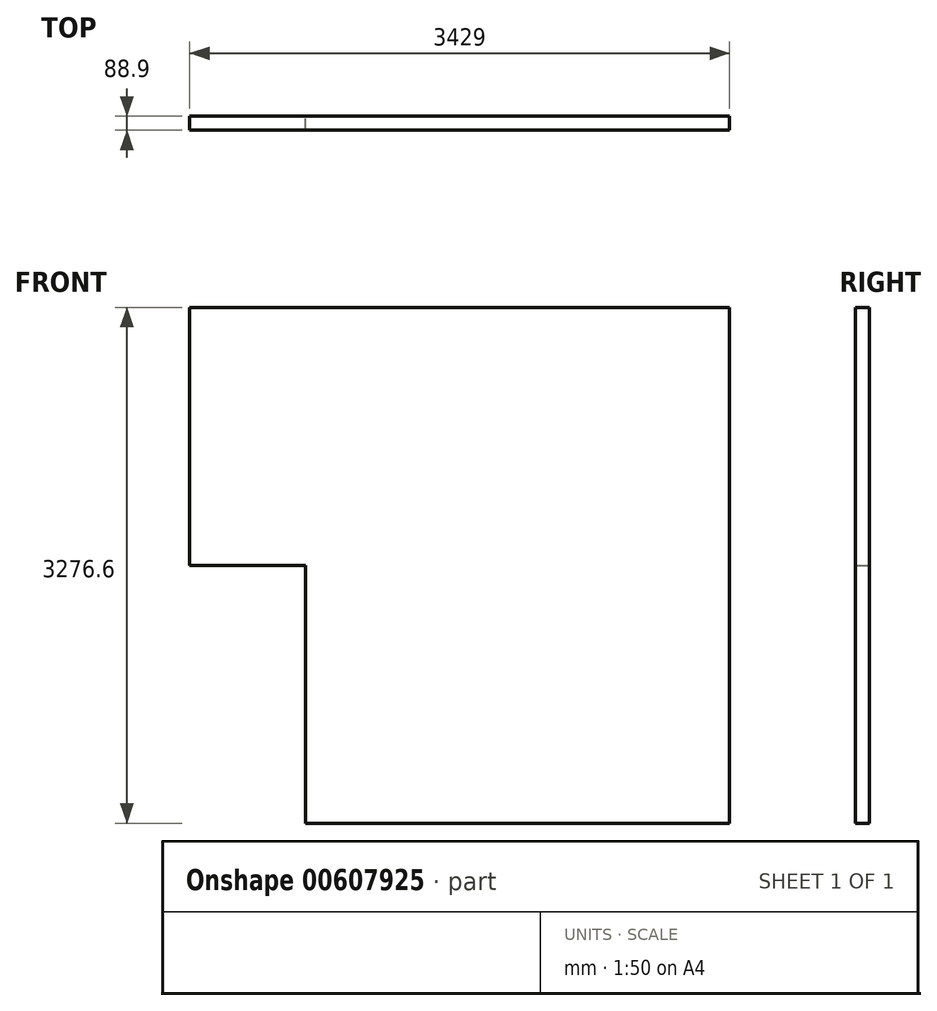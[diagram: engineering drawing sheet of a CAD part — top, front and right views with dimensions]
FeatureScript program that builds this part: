
annotation { "Feature Type Name" : "Feature", "Feature Type Description" : "" }
export const myFeature = defineFeature(function(context is Context, id is Id, definition is map)
    precondition{}
    {
        {
            var Q0;
            Q0=qCreatedBy(makeId("Front.planeOp"),FACE);
            var sketch = newSketch(context, id + "F0", { "sketchPlane" : qUnion([Q0])});
            skLineSegment(sketch, "E0.bottom", {"start": v(1808.65, -1638.3) * mm, "end": v(-883.75, -1638.3) * mm});
            skLineSegment(sketch, "E0.top", {"start": v(1808.65, 1638.3) * mm, "end": v(-1620.35, 1638.3) * mm});
            skLineSegment(sketch, "E0.left", {"start": v(1808.65, -1638.3) * mm, "end": v(1808.65, 1638.3) * mm});
            skLineSegment(sketch, "E0.right", {"start": v(-1620.35, 0) * mm, "end": v(-1620.35, 1638.3) * mm});
            skLineSegment(sketch, "E1", {"start": v(-1620.88, 0) * mm, "end": v(-883.75, 0) * mm});
            skPoint(sketch, "E1.endSnap0", {"position": v(-1620.35, 0) * mm});
            skLineSegment(sketch, "E2", {"start": v(-883.75, 0) * mm, "end": v(-883.75, -1638.3) * mm});
            skSolve(sketch);
        }
        {
            var Q0;
            Q0=makeQuery(id+"F0.imprint","IMPRINT",FACE,{"disambiguationData":[TD([[makeQuery(id+"F0.imprint","IMPRINT",EDGE,{"derivedFrom":sQuery(id+"F0.wireOp",EDGE,"E0.bottom")}),-1.0]])]});
            extrude(context, id + "F1", {"entities" : qUnion([Q0]), "depth" : 88.9 * mm, "offsetDistance" : 25.4 * mm});
        }
    });
